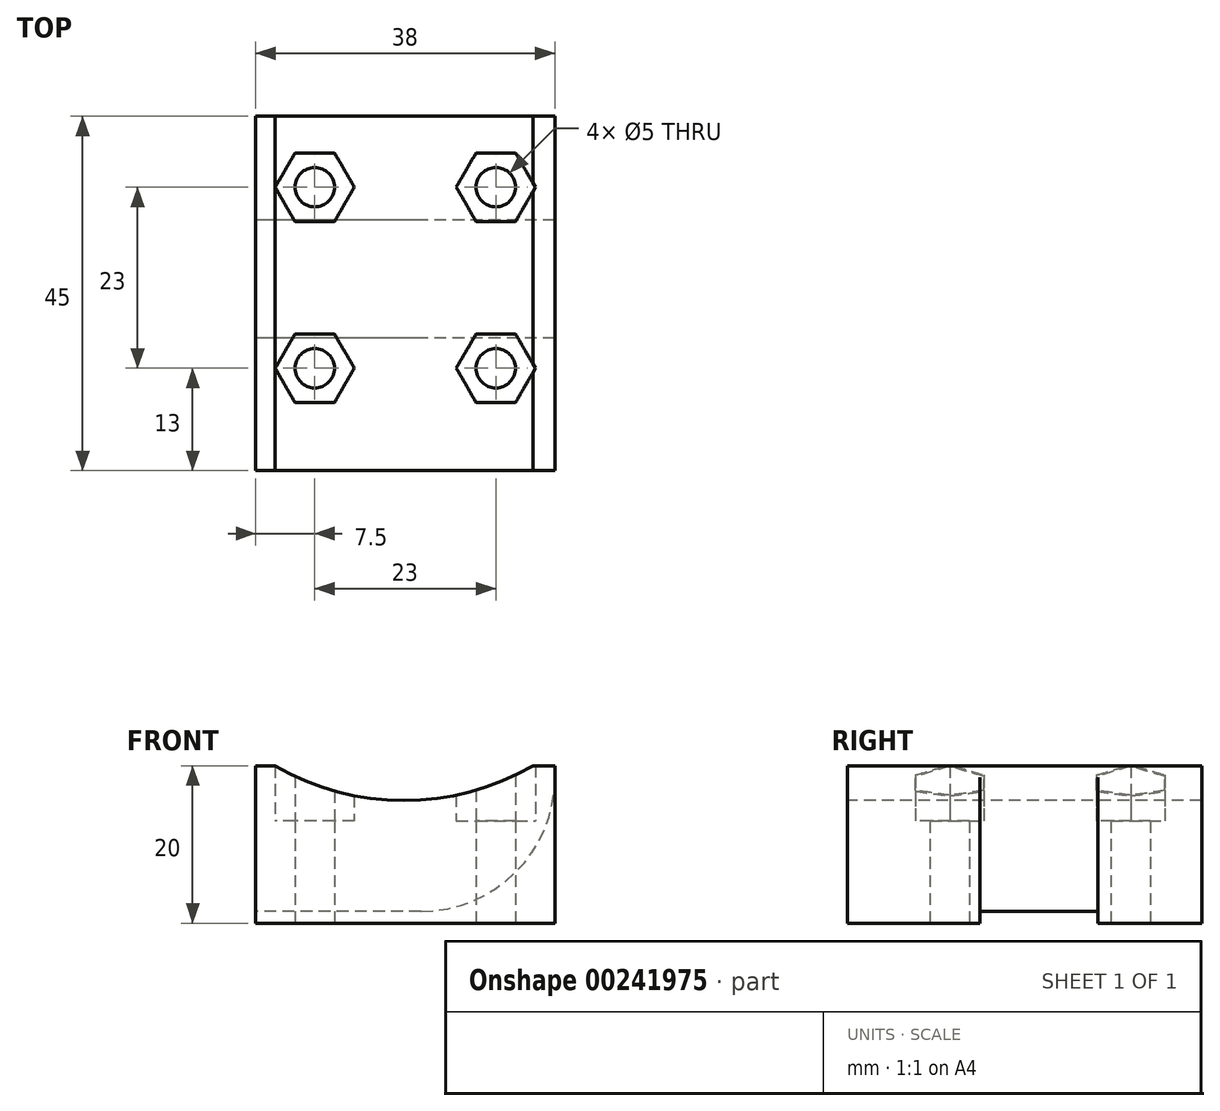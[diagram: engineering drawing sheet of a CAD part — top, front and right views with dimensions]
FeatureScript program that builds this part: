
annotation { "Feature Type Name" : "Feature", "Feature Type Description" : "" }
export const myFeature = defineFeature(function(context is Context, id is Id, definition is map)
    precondition{}
    {
        {
            var Q0;
            Q0=qCreatedBy(makeId("Top.planeOp"),FACE);
            var sketch = newSketch(context, id + "F0", { "sketchPlane" : qUnion([Q0])});
            skCircle(sketch, "E0", {"center": v(7.5, -9) * mm, "radius": 2.5 * mm});
            skCircle(sketch, "E1", {"center": v(30.5, -9) * mm, "radius": 2.5 * mm});
            skCircle(sketch, "E2", {"center": v(30.5, -32) * mm, "radius": 2.5 * mm});
            skCircle(sketch, "E3", {"center": v(7.5, -32) * mm, "radius": 2.5 * mm});
            skLineSegment(sketch, "E4.bottom", {"start": v(0, 0) * mm, "end": v(38, 0) * mm});
            skLineSegment(sketch, "E4.top", {"start": v(0, -45) * mm, "end": v(38, -45) * mm});
            skLineSegment(sketch, "E4.left", {"start": v(0, 0) * mm, "end": v(0, -45) * mm});
            skLineSegment(sketch, "E4.right", {"start": v(38, 0) * mm, "end": v(38, -45) * mm});
            skCircle(sketch, "E5.cCircle", {"center": v(7.5, -9) * mm, "radius": 4.35 * mm, "construction": true});
            skLineSegment(sketch, "E5.0", {"start": v(4.99, -4.65) * mm, "end": v(10.01, -4.65) * mm});
            skLineSegment(sketch, "E5.1", {"start": v(10.01, -4.65) * mm, "end": v(12.52, -9) * mm});
            skLineSegment(sketch, "E5.2", {"start": v(12.52, -9) * mm, "end": v(10.01, -13.35) * mm});
            skLineSegment(sketch, "E5.3", {"start": v(10.01, -13.35) * mm, "end": v(4.99, -13.35) * mm});
            skLineSegment(sketch, "E5.4", {"start": v(4.99, -13.35) * mm, "end": v(2.48, -9) * mm});
            skLineSegment(sketch, "E5.5", {"start": v(2.48, -9) * mm, "end": v(4.99, -4.65) * mm});
            skPoint(sketch, "E5.0.midPoint", {"position": v(7.5, -4.65) * mm});
            skCircle(sketch, "E6.cCircle", {"center": v(30.5, -9) * mm, "radius": 4.35 * mm, "construction": true});
            skLineSegment(sketch, "E6.0", {"start": v(27.99, -4.65) * mm, "end": v(33.01, -4.65) * mm});
            skLineSegment(sketch, "E6.1", {"start": v(33.01, -4.65) * mm, "end": v(35.52, -9) * mm});
            skLineSegment(sketch, "E6.2", {"start": v(35.52, -9) * mm, "end": v(33.01, -13.35) * mm});
            skLineSegment(sketch, "E6.3", {"start": v(33.01, -13.35) * mm, "end": v(27.99, -13.35) * mm});
            skLineSegment(sketch, "E6.4", {"start": v(27.99, -13.35) * mm, "end": v(25.48, -9) * mm});
            skLineSegment(sketch, "E6.5", {"start": v(25.48, -9) * mm, "end": v(27.99, -4.65) * mm});
            skPoint(sketch, "E6.0.midPoint", {"position": v(30.5, -4.65) * mm});
            skCircle(sketch, "E7.cCircle", {"center": v(30.5, -32) * mm, "radius": 4.35 * mm, "construction": true});
            skLineSegment(sketch, "E7.0", {"start": v(33.01, -36.35) * mm, "end": v(27.99, -36.35) * mm});
            skLineSegment(sketch, "E7.1", {"start": v(27.99, -36.35) * mm, "end": v(25.48, -32) * mm});
            skLineSegment(sketch, "E7.2", {"start": v(25.48, -32) * mm, "end": v(27.99, -27.65) * mm});
            skLineSegment(sketch, "E7.3", {"start": v(27.99, -27.65) * mm, "end": v(33.01, -27.65) * mm});
            skLineSegment(sketch, "E7.4", {"start": v(33.01, -27.65) * mm, "end": v(35.52, -32) * mm});
            skLineSegment(sketch, "E7.5", {"start": v(35.52, -32) * mm, "end": v(33.01, -36.35) * mm});
            skPoint(sketch, "E7.0.midPoint", {"position": v(30.5, -36.35) * mm});
            skCircle(sketch, "E8.cCircle", {"center": v(7.5, -32) * mm, "radius": 4.35 * mm, "construction": true});
            skLineSegment(sketch, "E8.0", {"start": v(10.01, -36.35) * mm, "end": v(4.99, -36.35) * mm});
            skLineSegment(sketch, "E8.1", {"start": v(4.99, -36.35) * mm, "end": v(2.48, -32) * mm});
            skLineSegment(sketch, "E8.2", {"start": v(2.48, -32) * mm, "end": v(4.99, -27.65) * mm});
            skLineSegment(sketch, "E8.3", {"start": v(4.99, -27.65) * mm, "end": v(10.01, -27.65) * mm});
            skLineSegment(sketch, "E8.4", {"start": v(10.01, -27.65) * mm, "end": v(12.52, -32) * mm});
            skLineSegment(sketch, "E8.5", {"start": v(12.52, -32) * mm, "end": v(10.01, -36.35) * mm});
            skPoint(sketch, "E8.0.midPoint", {"position": v(7.5, -36.35) * mm});
            skSolve(sketch);
        }
        {
            var Q0;
            Q0=makeQuery(id+"F0.imprint","IMPRINT",FACE,{"disambiguationData":[TD([[makeQuery(id+"F0.imprint","IMPRINT",EDGE,{"derivedFrom":sQuery(id+"F0.wireOp",EDGE,"E4.bottom")}),-1.0]])]});
            extrude(context, id + "F1", {"entities" : qUnion([Q0]), "depth" : 20 * mm});
        }
        {
            var Q0;
            Q0=makeQuery(id+"F0.imprint","IMPRINT",FACE,{"disambiguationData":[TD([[makeQuery(id+"F0.imprint","IMPRINT",EDGE,{"derivedFrom":sQuery(id+"F0.wireOp",EDGE,"E0")}),-1.0]])]});
            extrude(context, id + "F2", {"entities" : qUnion([Q0]), "operationType" : NewBodyOperationType.ADD, "depth" : 13 * mm});
        }
        {
            var Q0;
            Q0=makeQuery(id+"F0.imprint","IMPRINT",FACE,{"disambiguationData":[TD([[makeQuery(id+"F0.imprint","IMPRINT",EDGE,{"derivedFrom":sQuery(id+"F0.wireOp",EDGE,"E1")}),-1.0]])]});
            extrude(context, id + "F3", {"entities" : qUnion([Q0]), "operationType" : NewBodyOperationType.ADD, "depth" : 13 * mm});
        }
        {
            var Q0;
            Q0=makeQuery(id+"F0.imprint","IMPRINT",FACE,{"disambiguationData":[TD([[makeQuery(id+"F0.imprint","IMPRINT",EDGE,{"derivedFrom":sQuery(id+"F0.wireOp",EDGE,"E3")}),-1.0]])]});
            extrude(context, id + "F4", {"entities" : qUnion([Q0]), "operationType" : NewBodyOperationType.ADD, "depth" : 13 * mm});
        }
        {
            var Q0;
            Q0=makeQuery(id+"F0.imprint","IMPRINT",FACE,{"disambiguationData":[TD([[makeQuery(id+"F0.imprint","IMPRINT",EDGE,{"derivedFrom":sQuery(id+"F0.wireOp",EDGE,"E2")}),-1.0]])]});
            extrude(context, id + "F5", {"entities" : qUnion([Q0]), "operationType" : NewBodyOperationType.ADD, "depth" : 13 * mm});
        }
        {
            var Q0;
            Q0=qCreatedBy(makeId("Right.planeOp"),FACE);
            var sketch = newSketch(context, id + "F6", { "sketchPlane" : qUnion([Q0])});
            skLineSegment(sketch, "E9.bottom", {"start": v(-13.2, 1.5) * mm, "end": v(-28.2, 1.5) * mm});
            skLineSegment(sketch, "E9.top", {"start": v(-13.2, -18.5) * mm, "end": v(-28.2, -18.5) * mm});
            skLineSegment(sketch, "E9.left", {"start": v(-13.2, 1.5) * mm, "end": v(-13.2, -18.5) * mm});
            skLineSegment(sketch, "E9.right", {"start": v(-28.2, 1.5) * mm, "end": v(-28.2, -18.5) * mm});
            skSolve(sketch);
        }
        {
            var Q0;
            Q0 = qSketchRegion(id + "F6", true);
            extrude(context, id + "F7", {"entities" : qUnion([Q0]), "operationType" : NewBodyOperationType.REMOVE, "depth" : 40.2 * mm});
        }
        {
            var Q0;
            Q0=makeQuery(id+"F1.opExtrude","SWEPT_FACE",FACE,{"disambiguationData":[OSD([sQuery(id+"F0.wireOp",EDGE,"E4.top")])]});
            cPlane(context, id + "F8", {"entities" : qUnion([Q0]), "cplaneType" : CPlaneType.OFFSET, "offset" : 25 * mm, "width" : 150 * mm, "height" : 150 * mm});
        }
        {
            var Q0;
            Q0=qCreatedBy(id+"F8.planeOp",FACE);
            var sketch = newSketch(context, id + "F9", { "sketchPlane" : qUnion([Q0])});
            skCircle(sketch, "E10", {"center": v(18.82, 48.07) * mm, "radius": 32.5 * mm});
            skSolve(sketch);
        }
        {
            var Q0;
            Q0=makeQuery(id+"F9.imprint","IMPRINT",FACE,{"disambiguationData":[TD([[makeQuery(id+"F9.imprint","IMPRINT",EDGE,{"derivedFrom":sQuery(id+"F9.wireOp",EDGE,"E10")}),1.0]])]});
            extrude(context, id + "F10", {"entities" : qUnion([Q0]), "operationType" : NewBodyOperationType.REMOVE, "oppositeDirection" : true, "depth" : 102.8 * mm});
        }
        {
            var Q0;
            Q0=makeQuery(id+"F7.boolean.opBoolean","INTERSECT",EDGE,{"derivedFrom":[makeQuery(id+"F1.opExtrude","SWEPT_FACE",FACE,{"disambiguationData":[OSD([sQuery(id+"F0.wireOp",EDGE,"E4.right")])]}),makeQuery(id+"F7.opExtrude","SWEPT_FACE",FACE,{"disambiguationData":[OSD([sQuery(id+"F6.wireOp",EDGE,"E9.bottom")])]})]});
            var Q1;
            Q1=makeQuery(id+"F7.boolean.opBoolean","COPY",EDGE,{"derivedFrom":makeQuery(id+"F7.opExtrude","CAP_EDGE",EDGE,{"disambiguationData":[OSD([sQuery(id+"F6.wireOp",EDGE,"E9.bottom")])],"isStart":true})});
            fillet(context, id + "F11", {"entities" : qUnion([Q0, Q1]), "radius" : 17 * mm, "tangentPropagation" : true, "allowEdgeOverflow" : false});
        }
    });
